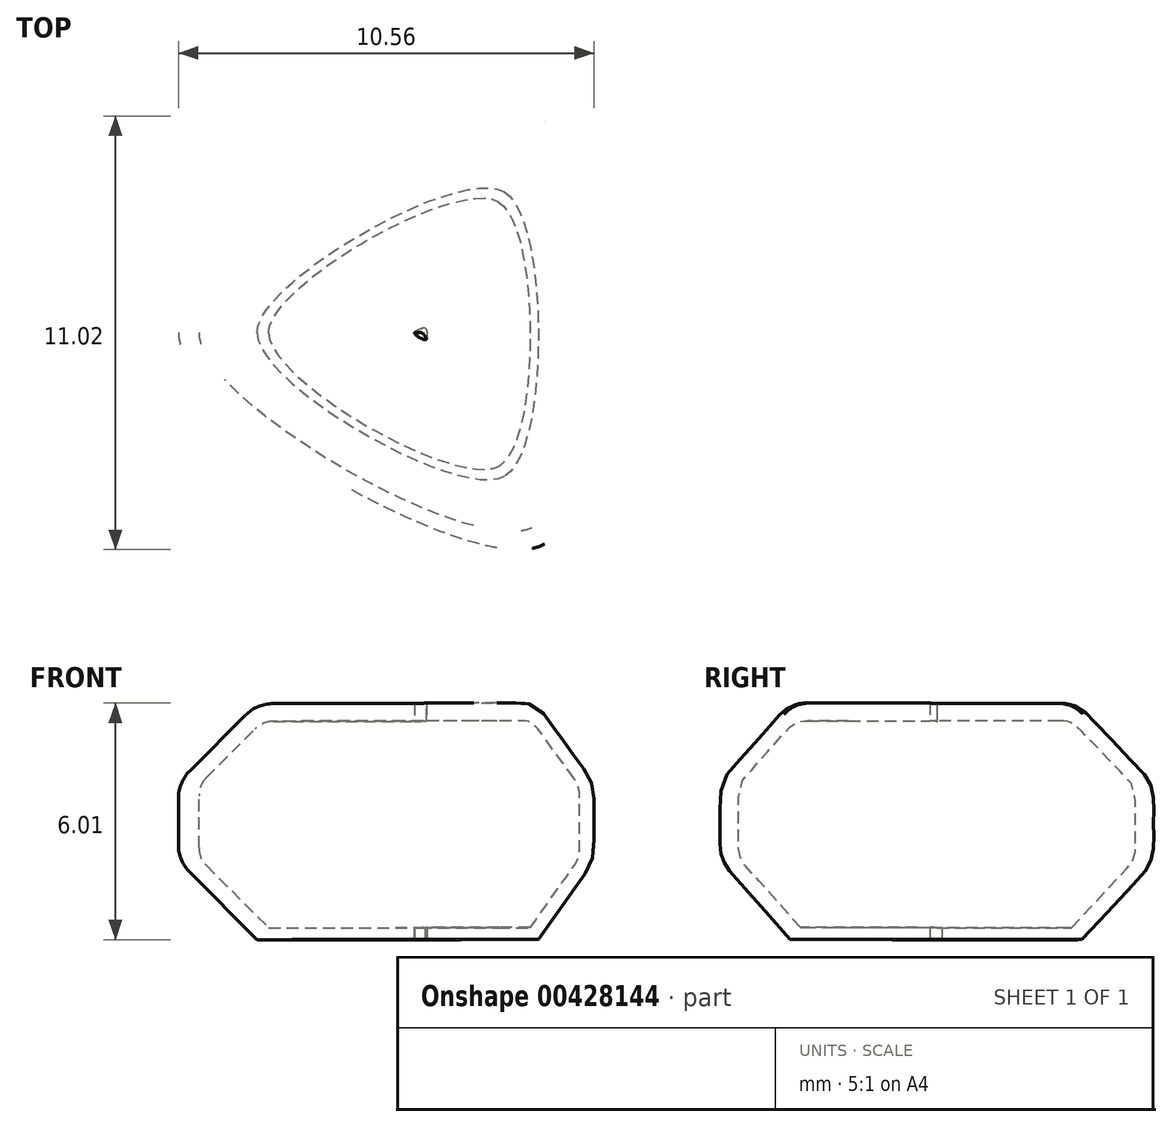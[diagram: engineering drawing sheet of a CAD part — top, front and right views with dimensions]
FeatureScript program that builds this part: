
annotation { "Feature Type Name" : "Feature", "Feature Type Description" : "" }
export const myFeature = defineFeature(function(context is Context, id is Id, definition is map)
    precondition{}
    {
        {
            var Q0;
            Q0=qCreatedBy(makeId("Front.planeOp"),FACE);
            var sketch = newSketch(context, id + "F0", { "sketchPlane" : qUnion([Q0])});
            skLineSegment(sketch, "E0", {"start": v(0, 0) * mm, "end": v(0, 3.09) * mm});
            skSolve(sketch);
        }
        {
            var Q0;
            Q0=sQuery(id+"F0.wireOp",EDGE,"E0");
            cPlane(context, id + "F1", {"entities" : qUnion([Q0]), "cplaneType" : CPlaneType.LINE_ANGLE, "offset" : 0 * mm, "angle" : 150 * degree, "width" : 150 * mm, "height" : 150 * mm});
        }
        {
            var Q0;
            Q0=sQuery(id+"F0.wireOp",EDGE,"E0");
            cPlane(context, id + "F2", {"entities" : qUnion([Q0]), "cplaneType" : CPlaneType.LINE_ANGLE, "offset" : 25 * mm, "angle" : 30 * degree, "width" : 150 * mm, "height" : 150 * mm});
        }
        {
            var Q0;
            Q0=qCreatedBy(id+"F1.planeOp",FACE);
            var sketch = newSketch(context, id + "F3", { "sketchPlane" : qUnion([Q0])});
            skLineSegment(sketch, "E1", {"start": v(-0.14, -2.9) * mm, "end": v(-4.14, -2.9) * mm});
            skLineSegment(sketch, "E2", {"start": v(-6.2, -0.52) * mm, "end": v(-6.2, 0.61) * mm});
            skLineSegment(sketch, "E3", {"start": v(-3.6, 3.1) * mm, "end": v(0.01, 3.1) * mm});
            skLineSegment(sketch, "E4", {"start": v(-5.88, 1.35) * mm, "end": v(-4.28, 2.83) * mm});
            skLineSegment(sketch, "E5", {"start": v(-5.89, -1.25) * mm, "end": v(-4.14, -2.9) * mm});
            skPoint(sketch, "E6.visualSharp", {"position": v(-3.99, 3.1) * mm});
            skArc(sketch, "E6.filletArc", {"start": v(-3.6, 3.1) * mm, "mid": v(-3.96, 3.02) * mm, "end": v(-4.28, 2.83) * mm});
            skPoint(sketch, "E7.visualSharp", {"position": v(-6.2, 1.05) * mm});
            skArc(sketch, "E7.filletArc", {"start": v(-5.88, 1.35) * mm, "mid": v(-6.12, 1.01) * mm, "end": v(-6.2, 0.61) * mm});
            skPoint(sketch, "E8.visualSharp", {"position": v(-6.2, -0.95) * mm});
            skArc(sketch, "E8.filletArc", {"start": v(-6.2, -0.52) * mm, "mid": v(-6.12, -0.92) * mm, "end": v(-5.89, -1.25) * mm});
            skLineSegment(sketch, "E9", {"start": v(-5.68, -0.59) * mm, "end": v(-5.68, 0.67) * mm});
            skLineSegment(sketch, "E10", {"start": v(-3.6, 2.64) * mm, "end": v(0.01, 2.64) * mm});
            skLineSegment(sketch, "E11", {"start": v(-5.48, -1.06) * mm, "end": v(-3.85, -2.6) * mm});
            skLineSegment(sketch, "E12", {"start": v(-5.47, 1.15) * mm, "end": v(-4.04, 2.47) * mm});
            skLineSegment(sketch, "E13", {"start": v(-3.85, -2.6) * mm, "end": v(-0.14, -2.6) * mm});
            skPoint(sketch, "E14.visualSharp", {"position": v(-3.86, 2.64) * mm});
            skArc(sketch, "E14.filletArc", {"start": v(-3.6, 2.64) * mm, "mid": v(-3.84, 2.6) * mm, "end": v(-4.04, 2.47) * mm});
            skPoint(sketch, "E15.visualSharp", {"position": v(-5.68, 0.96) * mm});
            skArc(sketch, "E15.filletArc", {"start": v(-5.47, 1.15) * mm, "mid": v(-5.63, 0.93) * mm, "end": v(-5.68, 0.67) * mm});
            skPoint(sketch, "E16.visualSharp", {"position": v(-5.68, -0.86) * mm});
            skArc(sketch, "E16.filletArc", {"start": v(-5.68, -0.59) * mm, "mid": v(-5.63, -0.84) * mm, "end": v(-5.48, -1.06) * mm});
            skLineSegment(sketch, "E17", {"start": v(0.01, 3.1) * mm, "end": v(0.01, 2.64) * mm});
            skLineSegment(sketch, "E18", {"start": v(-0.14, -2.6) * mm, "end": v(-0.14, -2.9) * mm});
            skSolve(sketch);
        }
        {
            var Q0;
            Q0=qCreatedBy(id+"F2.planeOp",FACE);
            var sketch = newSketch(context, id + "F4", { "sketchPlane" : qUnion([Q0])});
            skLineSegment(sketch, "E19", {"start": v(-0.2, -2.9) * mm, "end": v(-4.2, -2.9) * mm});
            skLineSegment(sketch, "E20", {"start": v(-6.2, -0.49) * mm, "end": v(-6.2, 0.68) * mm});
            skLineSegment(sketch, "E21", {"start": v(-3.79, 3.1) * mm, "end": v(-0.2, 3.1) * mm});
            skLineSegment(sketch, "E22", {"start": v(-5.9, 1.4) * mm, "end": v(-4.5, 2.8) * mm});
            skLineSegment(sketch, "E23", {"start": v(-5.9, -1.2) * mm, "end": v(-4.2, -2.9) * mm});
            skPoint(sketch, "E24.visualSharp", {"position": v(-4.2, 3.1) * mm});
            skArc(sketch, "E24.filletArc", {"start": v(-3.79, 3.1) * mm, "mid": v(-4.17, 3.02) * mm, "end": v(-4.5, 2.8) * mm});
            skPoint(sketch, "E25.visualSharp", {"position": v(-6.2, 1.1) * mm});
            skArc(sketch, "E25.filletArc", {"start": v(-5.9, 1.4) * mm, "mid": v(-6.12, 1.07) * mm, "end": v(-6.2, 0.68) * mm});
            skPoint(sketch, "E26.visualSharp", {"position": v(-6.2, -0.9) * mm});
            skArc(sketch, "E26.filletArc", {"start": v(-6.2, -0.49) * mm, "mid": v(-6.12, -0.87) * mm, "end": v(-5.9, -1.2) * mm});
            skLineSegment(sketch, "E27", {"start": v(-5.68, -0.56) * mm, "end": v(-5.68, 0.76) * mm});
            skLineSegment(sketch, "E28", {"start": v(-3.79, 2.65) * mm, "end": v(-0.2, 2.65) * mm});
            skLineSegment(sketch, "E29", {"start": v(-5.49, -1.02) * mm, "end": v(-3.9, -2.6) * mm});
            skLineSegment(sketch, "E30", {"start": v(-5.49, 1.22) * mm, "end": v(-4.25, 2.46) * mm});
            skLineSegment(sketch, "E31", {"start": v(-3.9, -2.6) * mm, "end": v(-0.2, -2.6) * mm});
            skPoint(sketch, "E32.visualSharp", {"position": v(-4.06, 2.65) * mm});
            skArc(sketch, "E32.filletArc", {"start": v(-3.79, 2.65) * mm, "mid": v(-4.04, 2.6) * mm, "end": v(-4.25, 2.46) * mm});
            skPoint(sketch, "E33.visualSharp", {"position": v(-5.68, 1.02) * mm});
            skArc(sketch, "E33.filletArc", {"start": v(-5.49, 1.22) * mm, "mid": v(-5.63, 1) * mm, "end": v(-5.68, 0.76) * mm});
            skPoint(sketch, "E34.visualSharp", {"position": v(-5.68, -0.83) * mm});
            skArc(sketch, "E34.filletArc", {"start": v(-5.68, -0.56) * mm, "mid": v(-5.63, -0.8) * mm, "end": v(-5.49, -1.02) * mm});
            skLineSegment(sketch, "E35", {"start": v(-0.2, 3.1) * mm, "end": v(-0.2, 2.65) * mm});
            skLineSegment(sketch, "E36", {"start": v(-0.2, -2.6) * mm, "end": v(-0.2, -2.9) * mm});
            skSolve(sketch);
        }
        {
            var Q0;
            Q0=qCreatedBy(makeId("Front.planeOp"),FACE);
            var sketch = newSketch(context, id + "F5", { "sketchPlane" : qUnion([Q0])});
            skLineSegment(sketch, "E37", {"start": v(-0.2, -2.91) * mm, "end": v(-4.2, -2.91) * mm});
            skLineSegment(sketch, "E38", {"start": v(-6.2, -0.5) * mm, "end": v(-6.2, 0.67) * mm});
            skLineSegment(sketch, "E39", {"start": v(-3.79, 3.09) * mm, "end": v(-0.2, 3.09) * mm});
            skLineSegment(sketch, "E40", {"start": v(-5.9, 1.38) * mm, "end": v(-4.5, 2.8) * mm});
            skLineSegment(sketch, "E41", {"start": v(-5.9, -1.2) * mm, "end": v(-4.2, -2.91) * mm});
            skPoint(sketch, "E42.visualSharp", {"position": v(-4.2, 3.09) * mm});
            skArc(sketch, "E42.filletArc", {"start": v(-3.79, 3.09) * mm, "mid": v(-4.17, 3.01) * mm, "end": v(-4.5, 2.8) * mm});
            skPoint(sketch, "E43.visualSharp", {"position": v(-6.2, 1.09) * mm});
            skArc(sketch, "E43.filletArc", {"start": v(-5.9, 1.38) * mm, "mid": v(-6.12, 1.06) * mm, "end": v(-6.2, 0.67) * mm});
            skPoint(sketch, "E44.visualSharp", {"position": v(-6.2, -0.91) * mm});
            skArc(sketch, "E44.filletArc", {"start": v(-6.2, -0.5) * mm, "mid": v(-6.12, -0.88) * mm, "end": v(-5.9, -1.2) * mm});
            skLineSegment(sketch, "E45", {"start": v(-5.68, -0.57) * mm, "end": v(-5.68, 0.75) * mm});
            skLineSegment(sketch, "E46", {"start": v(-3.79, 2.64) * mm, "end": v(-0.2, 2.64) * mm});
            skLineSegment(sketch, "E47", {"start": v(-5.49, -1.03) * mm, "end": v(-3.9, -2.61) * mm});
            skLineSegment(sketch, "E48", {"start": v(-5.49, 1.2) * mm, "end": v(-4.25, 2.45) * mm});
            skLineSegment(sketch, "E49", {"start": v(-3.9, -2.61) * mm, "end": v(-0.2, -2.61) * mm});
            skPoint(sketch, "E50.visualSharp", {"position": v(-4.06, 2.64) * mm});
            skArc(sketch, "E50.filletArc", {"start": v(-3.79, 2.64) * mm, "mid": v(-4.04, 2.59) * mm, "end": v(-4.25, 2.45) * mm});
            skPoint(sketch, "E51.visualSharp", {"position": v(-5.68, 1.02) * mm});
            skArc(sketch, "E51.filletArc", {"start": v(-5.49, 1.2) * mm, "mid": v(-5.63, 1) * mm, "end": v(-5.68, 0.75) * mm});
            skPoint(sketch, "E52.visualSharp", {"position": v(-5.68, -0.84) * mm});
            skArc(sketch, "E52.filletArc", {"start": v(-5.68, -0.57) * mm, "mid": v(-5.63, -0.82) * mm, "end": v(-5.49, -1.03) * mm});
            skLineSegment(sketch, "E53", {"start": v(-0.2, 3.09) * mm, "end": v(-0.2, 2.64) * mm});
            skLineSegment(sketch, "E54", {"start": v(-0.2, -2.61) * mm, "end": v(-0.2, -2.91) * mm});
            skSolve(sketch);
        }
        {
            var Q0;
            Q0=makeQuery(id+"F5.imprint","IMPRINT",FACE,{"disambiguationData":[TD([[makeQuery(id+"F5.imprint","IMPRINT",EDGE,{"derivedFrom":sQuery(id+"F5.wireOp",EDGE,"E37")}),-1.0]])]});
            var Q1;
            Q1=makeQuery(id+"F3.imprint","IMPRINT",FACE,{"disambiguationData":[TD([[makeQuery(id+"F3.imprint","IMPRINT",EDGE,{"derivedFrom":sQuery(id+"F3.wireOp",EDGE,"E1")}),-1.0]])]});
            loft(context, id + "F6", {"startCondition" : LoftEndDerivativeType.NORMAL_TO_PROFILE, "startMagnitude" : 1, "endCondition" : LoftEndDerivativeType.NORMAL_TO_PROFILE, "endMagnitude" : 1, "sheetProfilesArray" : [{ "sheetProfileEntities" : qUnion([Q0]) }, { "sheetProfileEntities" : qUnion([Q1]) }]});
        }
        {
            var Q1;
            Q1=makeQuery(id+"F6.opLoft","CAP_FACE",FACE,{"disambiguationData":[OSD([makeQuery(id+"F3.imprint","IMPRINT",FACE,{"disambiguationData":[TD([[makeQuery(id+"F3.imprint","IMPRINT",EDGE,{"derivedFrom":sQuery(id+"F3.wireOp",EDGE,"E1")}),-1.0]])]})])],"isStart":true});
            var Q2;
            Q2=makeQuery(id+"F4.imprint","IMPRINT",FACE,{"disambiguationData":[TD([[makeQuery(id+"F4.imprint","IMPRINT",EDGE,{"derivedFrom":sQuery(id+"F4.wireOp",EDGE,"E19")}),-1.0]])]});
            loft(context, id + "F7", {"operationType" : NewBodyOperationType.ADD, "startCondition" : LoftEndDerivativeType.NORMAL_TO_PROFILE, "startMagnitude" : 1, "endCondition" : LoftEndDerivativeType.NORMAL_TO_PROFILE, "endMagnitude" : 1, "sheetProfilesArray" : [{ "sheetProfileEntities" : qUnion([Q1]) }, { "sheetProfileEntities" : qUnion([Q2]) }]});
        }
        {
            var Q1;
            Q1=makeQuery(id+"F6.opLoft","CAP_FACE",FACE,{"disambiguationData":[OSD([makeQuery(id+"F5.imprint","IMPRINT",FACE,{"disambiguationData":[TD([[makeQuery(id+"F5.imprint","IMPRINT",EDGE,{"derivedFrom":sQuery(id+"F5.wireOp",EDGE,"E37")}),-1.0]])]})])],"isStart":true});
            var Q2;
            Q2=makeQuery(id+"F7.opLoft","CAP_FACE",FACE,{"disambiguationData":[OSD([makeQuery(id+"F4.imprint","IMPRINT",FACE,{"disambiguationData":[TD([[makeQuery(id+"F4.imprint","IMPRINT",EDGE,{"derivedFrom":sQuery(id+"F4.wireOp",EDGE,"E19")}),-1.0]])]})])],"isStart":true});
            loft(context, id + "F8", {"operationType" : NewBodyOperationType.ADD, "startCondition" : LoftEndDerivativeType.NORMAL_TO_PROFILE, "startMagnitude" : 1, "endCondition" : LoftEndDerivativeType.NORMAL_TO_PROFILE, "endMagnitude" : 1, "sheetProfilesArray" : [{ "sheetProfileEntities" : qUnion([Q1]) }, { "sheetProfileEntities" : qUnion([Q2]) }]});
        }
    });
